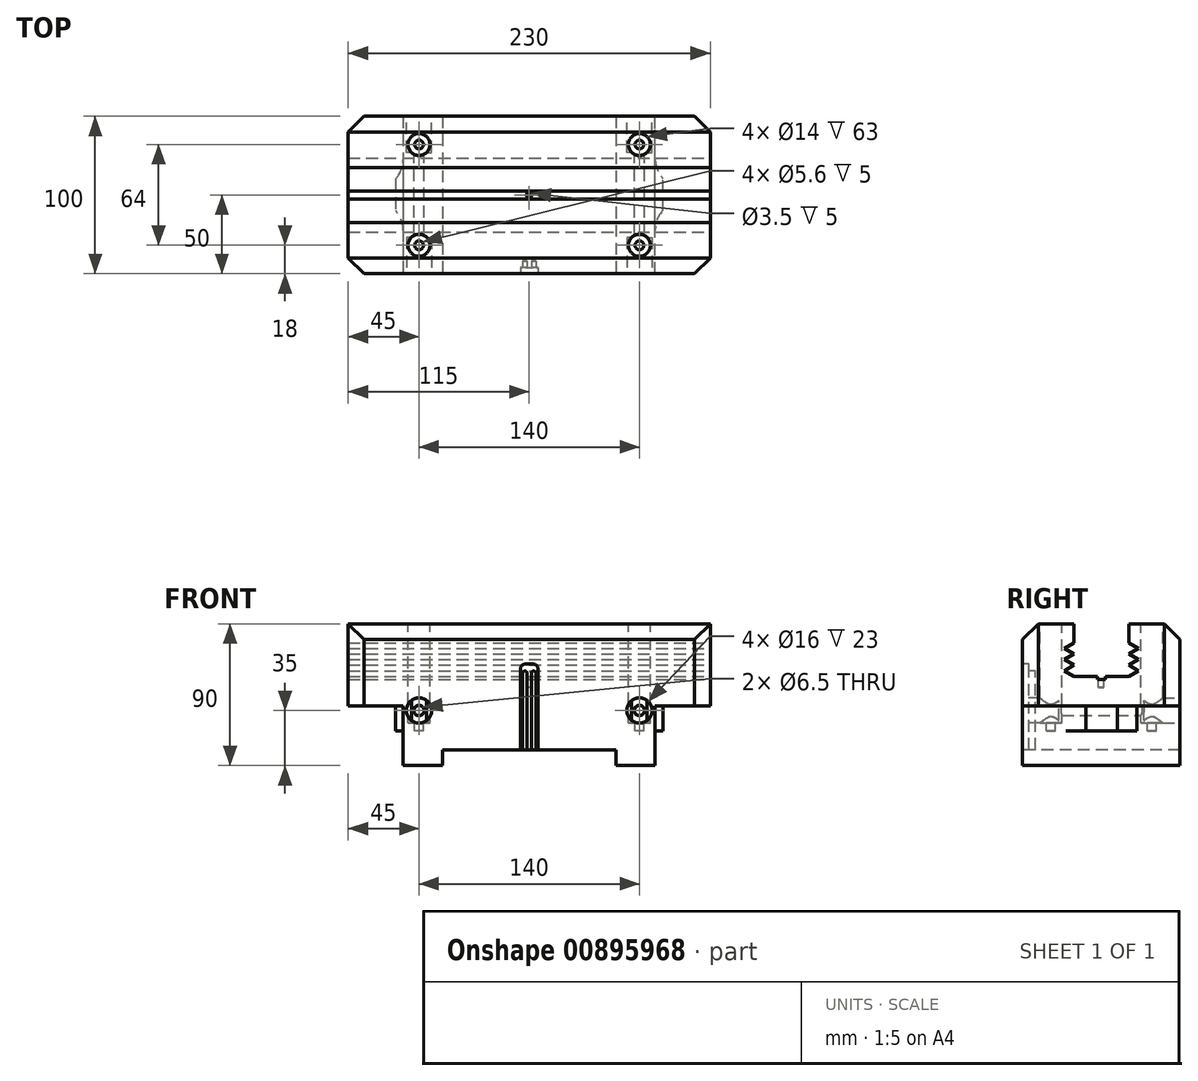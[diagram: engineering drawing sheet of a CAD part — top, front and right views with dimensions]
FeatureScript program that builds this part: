
annotation { "Feature Type Name" : "Feature", "Feature Type Description" : "" }
export const myFeature = defineFeature(function(context is Context, id is Id, definition is map)
    precondition{}
    {
        {
            var Q0;
            Q0=qCreatedBy(makeId("Top.planeOp"),FACE);
            var sketch = newSketch(context, id + "F0", { "sketchPlane" : qUnion([Q0])});
            skLineSegment(sketch, "E0.bottom", {"start": v(-115, 50) * mm, "end": v(115, 50) * mm});
            skLineSegment(sketch, "E0.top", {"start": v(-115, -50) * mm, "end": v(115, -50) * mm});
            skLineSegment(sketch, "E0.left", {"start": v(-115, 50) * mm, "end": v(-115, -50) * mm});
            skLineSegment(sketch, "E0.right", {"start": v(115, 50) * mm, "end": v(115, -50) * mm});
            skSolve(sketch);
        }
        {
            var Q0;
            Q0=makeQuery(id+"F0.imprint","IMPRINT",FACE,{"disambiguationData":[TD([[makeQuery(id+"F0.imprint","IMPRINT",EDGE,{"derivedFrom":sQuery(id+"F0.wireOp",EDGE,"E0.bottom")}),-1.0]])]});
            extrude(context, id + "F1", {"entities" : qUnion([Q0]), "oppositeDirection" : true, "depth" : 52 * mm, "offsetDistance" : 25 * mm});
        }
        {
            var Q0;
            Q0=makeQuery(id+"F1.opExtrude","SWEPT_FACE",FACE,{"disambiguationData":[OSD([sQuery(id+"F0.wireOp",EDGE,"E0.right")])]});
            var sketch = newSketch(context, id + "F2", { "sketchPlane" : qUnion([Q0])});
            skLineSegment(sketch, "E1", {"start": v(-17.5, 0) * mm, "end": v(17.5, 0) * mm});
            skLineSegment(sketch, "E2", {"start": v(-17.5, 0) * mm, "end": v(-17.5, -12) * mm});
            skLineSegment(sketch, "E3", {"start": v(-17.5, -12) * mm, "end": v(-23.52, -15.55) * mm});
            skLineSegment(sketch, "E4", {"start": v(-23.52, -15.55) * mm, "end": v(-17.5, -19.1) * mm});
            skLineSegment(sketch, "E5", {"start": v(-17.5, -19.1) * mm, "end": v(-23.52, -22.65) * mm});
            skLineSegment(sketch, "E6", {"start": v(-23.52, -22.65) * mm, "end": v(-17.5, -26.2) * mm});
            skLineSegment(sketch, "E7", {"start": v(-17.5, -26.2) * mm, "end": v(-23.52, -29.75) * mm});
            skLineSegment(sketch, "E8", {"start": v(-23.52, -29.75) * mm, "end": v(-17.5, -33.3) * mm});
            skLineSegment(sketch, "E9", {"start": v(17.5, 0) * mm, "end": v(17.5, -12) * mm});
            skLineSegment(sketch, "E10", {"start": v(17.5, -33.3) * mm, "end": v(23.52, -29.75) * mm});
            skLineSegment(sketch, "E11", {"start": v(23.52, -29.75) * mm, "end": v(17.5, -26.2) * mm});
            skLineSegment(sketch, "E12", {"start": v(17.5, -26.2) * mm, "end": v(23.52, -22.65) * mm});
            skLineSegment(sketch, "E13", {"start": v(23.52, -22.65) * mm, "end": v(17.5, -19.1) * mm});
            skLineSegment(sketch, "E14", {"start": v(17.5, -19.1) * mm, "end": v(23.52, -15.55) * mm});
            skLineSegment(sketch, "E15", {"start": v(23.52, -15.55) * mm, "end": v(17.5, -12) * mm});
            skLineSegment(sketch, "E16", {"start": v(-17.5, -33.3) * mm, "end": v(-2.5, -33.3) * mm});
            skLineSegment(sketch, "E17", {"start": v(17.5, -33.3) * mm, "end": v(2.5, -33.3) * mm});
            skLineSegment(sketch, "E18", {"start": v(-2.5, -33.3) * mm, "end": v(-2.5, -35.3) * mm});
            skLineSegment(sketch, "E19", {"start": v(2.5, -33.3) * mm, "end": v(2.5, -35.3) * mm});
            skLineSegment(sketch, "E20", {"start": v(2.5, -35.3) * mm, "end": v(-2.5, -35.3) * mm});
            skSolve(sketch);
        }
        {
            var Q0;
            Q0=makeQuery(id+"F2.imprint","IMPRINT",FACE,{"disambiguationData":[TD([[makeQuery(id+"F2.imprint","IMPRINT",EDGE,{"derivedFrom":sQuery(id+"F2.wireOp",EDGE,"E1")}),1.0]])]});
            extrude(context, id + "F3", {"entities" : qUnion([Q0]), "operationType" : NewBodyOperationType.REMOVE, "endBound" : BoundingType.UP_TO_NEXT, "oppositeDirection" : true, "depth" : 218 * mm, "offsetDistance" : 25 * mm});
        }
        {
            var Q0;
            Q0=makeQuery(id+"F1.opExtrude","CAP_EDGE",EDGE,{"disambiguationData":[OSD([sQuery(id+"F0.wireOp",EDGE,"E0.bottom")])],"isStart":true});
            var Q1;
            Q1=makeQuery(id+"F1.opExtrude","CAP_EDGE",EDGE,{"disambiguationData":[OSD([sQuery(id+"F0.wireOp",EDGE,"E0.top")])],"isStart":true});
            var Q2;
            Q2=makeQuery(id+"F1.opExtrude","SWEPT_EDGE",EDGE,{"disambiguationData":[OSD([sQuery(id+"F0.wireOp",EDGE,"E0.top"),sQuery(id+"F0.wireOp",EDGE,"E0.right")])]});
            var Q3;
            Q3=makeQuery(id+"F1.opExtrude","SWEPT_EDGE",EDGE,{"disambiguationData":[OSD([sQuery(id+"F0.wireOp",EDGE,"E0.bottom"),sQuery(id+"F0.wireOp",EDGE,"E0.right")])]});
            var Q4;
            Q4=makeQuery(id+"F1.opExtrude","SWEPT_EDGE",EDGE,{"disambiguationData":[OSD([sQuery(id+"F0.wireOp",EDGE,"E0.top"),sQuery(id+"F0.wireOp",EDGE,"E0.left")])]});
            var Q5;
            Q5=makeQuery(id+"F1.opExtrude","SWEPT_EDGE",EDGE,{"disambiguationData":[OSD([sQuery(id+"F0.wireOp",EDGE,"E0.bottom"),sQuery(id+"F0.wireOp",EDGE,"E0.left")])]});
            chamfer(context, id + "F4", {"entities" : qUnion([Q0, Q1, Q2, Q3, Q4, Q5]), "width" : 10 * mm, "tangentPropagation" : true});
        }
        {
            var Q0;
            Q0=makeQuery(id+"F1.opExtrude","CAP_FACE",FACE,{"disambiguationData":[OSD([sQuery(id+"F0.wireOp",EDGE,"E0.bottom"),sQuery(id+"F0.wireOp",EDGE,"E0.top"),sQuery(id+"F0.wireOp",EDGE,"E0.left"),sQuery(id+"F0.wireOp",EDGE,"E0.right")])],"isStart":false});
            var sketch = newSketch(context, id + "F5", { "sketchPlane" : qUnion([Q0])});
            skLineSegment(sketch, "E21", {"start": v(80, 50) * mm, "end": v(80, -50) * mm});
            skLineSegment(sketch, "E22", {"start": v(80, -50) * mm, "end": v(-80, -50) * mm});
            skLineSegment(sketch, "E23", {"start": v(-80, -50) * mm, "end": v(-80, 50) * mm});
            skLineSegment(sketch, "E24", {"start": v(-80, 50) * mm, "end": v(80, 50) * mm});
            skSolve(sketch);
        }
        {
            var Q0;
            Q0=makeQuery(id+"F5.imprint","IMPRINT",FACE,{"disambiguationData":[TD([[makeQuery(id+"F5.imprint","IMPRINT",EDGE,{"derivedFrom":sQuery(id+"F5.wireOp",EDGE,"E21")}),-1.0]])]});
            extrude(context, id + "F6", {"entities" : qUnion([Q0]), "operationType" : NewBodyOperationType.ADD, "depth" : 38 * mm, "offsetDistance" : 25 * mm});
        }
        {
            var Q0;
            {var subQ0=sQuery(id+"F0.wireOp",EDGE,"E0.bottom");var subQ1=sQuery(id+"F0.wireOp",EDGE,"E0.right");var subQ2=sQuery(id+"F0.wireOp",EDGE,"E0.left");Q0=makeQuery(id+"F3.boolean.opBoolean","SPLIT",FACE,{"disambiguationData":[TD([makeQuery(id+"F1.opExtrude","SWEPT_FACE",FACE,{"disambiguationData":[OSD([subQ0])]})])],"derivedFrom":makeQuery(id+"F1.opExtrude","CAP_FACE",FACE,{"disambiguationData":[OSD([subQ0,sQuery(id+"F0.wireOp",EDGE,"E0.top"),subQ2,subQ1])],"isStart":true})});}
            var sketch = newSketch(context, id + "F7", { "sketchPlane" : qUnion([Q0])});
            skCircle(sketch, "E25", {"center": v(70, -32) * mm, "radius": 7 * mm});
            skCircle(sketch, "E26", {"center": v(-70, -32) * mm, "radius": 7 * mm});
            skCircle(sketch, "E27", {"center": v(-70, 32) * mm, "radius": 7 * mm});
            skCircle(sketch, "E28", {"center": v(70, 32) * mm, "radius": 7 * mm});
            skCircle(sketch, "E29", {"center": v(-70, 32) * mm, "radius": 2.8 * mm});
            skCircle(sketch, "E30", {"center": v(70, 32) * mm, "radius": 2.8 * mm});
            skCircle(sketch, "E31", {"center": v(70, -32) * mm, "radius": 2.8 * mm});
            skCircle(sketch, "E32", {"center": v(-70, -32) * mm, "radius": 2.8 * mm});
            skSolve(sketch);
        }
        {
            var Q0;
            Q0 = qSketchRegion(id + "F7", true);
            extrude(context, id + "F8", {"entities" : qUnion([Q0]), "operationType" : NewBodyOperationType.REMOVE, "oppositeDirection" : true, "depth" : 63 * mm, "offsetDistance" : 25 * mm});
        }
        {
            var Q0;
            {var subQ0=sQuery(id+"F0.wireOp",EDGE,"E0.bottom");var subQ1=sQuery(id+"F0.wireOp",EDGE,"E0.right");var subQ2=sQuery(id+"F0.wireOp",EDGE,"E0.left");Q0=makeQuery(id+"F8.boolean.opBoolean","SPLIT",FACE,{"disambiguationData":[TD([makeQuery(id+"F8.opExtrude","SWEPT_FACE",FACE,{"disambiguationData":[OSD([sQuery(id+"F7.wireOp",EDGE,"E30")])]})])],"derivedFrom":makeQuery(id+"F3.boolean.opBoolean","SPLIT",FACE,{"disambiguationData":[TD([makeQuery(id+"F1.opExtrude","SWEPT_FACE",FACE,{"disambiguationData":[OSD([subQ0])]})])],"derivedFrom":makeQuery(id+"F1.opExtrude","CAP_FACE",FACE,{"disambiguationData":[OSD([subQ0,sQuery(id+"F0.wireOp",EDGE,"E0.top"),subQ2,subQ1])],"isStart":true})})});}
            var Q1;
            {var subQ0=sQuery(id+"F0.wireOp",EDGE,"E0.bottom");var subQ1=sQuery(id+"F0.wireOp",EDGE,"E0.right");var subQ2=sQuery(id+"F0.wireOp",EDGE,"E0.left");Q1=makeQuery(id+"F8.boolean.opBoolean","SPLIT",FACE,{"disambiguationData":[TD([makeQuery(id+"F8.opExtrude","SWEPT_FACE",FACE,{"disambiguationData":[OSD([sQuery(id+"F7.wireOp",EDGE,"E29")])]})])],"derivedFrom":makeQuery(id+"F3.boolean.opBoolean","SPLIT",FACE,{"disambiguationData":[TD([makeQuery(id+"F1.opExtrude","SWEPT_FACE",FACE,{"disambiguationData":[OSD([subQ0])]})])],"derivedFrom":makeQuery(id+"F1.opExtrude","CAP_FACE",FACE,{"disambiguationData":[OSD([subQ0,sQuery(id+"F0.wireOp",EDGE,"E0.top"),subQ2,subQ1])],"isStart":true})})});}
            var Q2;
            {var subQ0=sQuery(id+"F0.wireOp",EDGE,"E0.top");var subQ1=sQuery(id+"F0.wireOp",EDGE,"E0.left");var subQ2=sQuery(id+"F0.wireOp",EDGE,"E0.right");Q2=makeQuery(id+"F8.boolean.opBoolean","SPLIT",FACE,{"disambiguationData":[TD([makeQuery(id+"F8.opExtrude","SWEPT_FACE",FACE,{"disambiguationData":[OSD([sQuery(id+"F7.wireOp",EDGE,"E32")])]})])],"derivedFrom":makeQuery(id+"F3.boolean.opBoolean","SPLIT",FACE,{"disambiguationData":[TD([makeQuery(id+"F1.opExtrude","SWEPT_FACE",FACE,{"disambiguationData":[OSD([subQ0])]})])],"derivedFrom":makeQuery(id+"F1.opExtrude","CAP_FACE",FACE,{"disambiguationData":[OSD([sQuery(id+"F0.wireOp",EDGE,"E0.bottom"),subQ0,subQ1,subQ2])],"isStart":true})})});}
            var Q3;
            {var subQ0=sQuery(id+"F0.wireOp",EDGE,"E0.top");var subQ1=sQuery(id+"F0.wireOp",EDGE,"E0.left");var subQ2=sQuery(id+"F0.wireOp",EDGE,"E0.right");Q3=makeQuery(id+"F8.boolean.opBoolean","SPLIT",FACE,{"disambiguationData":[TD([makeQuery(id+"F8.opExtrude","SWEPT_FACE",FACE,{"disambiguationData":[OSD([sQuery(id+"F7.wireOp",EDGE,"E31")])]})])],"derivedFrom":makeQuery(id+"F3.boolean.opBoolean","SPLIT",FACE,{"disambiguationData":[TD([makeQuery(id+"F1.opExtrude","SWEPT_FACE",FACE,{"disambiguationData":[OSD([subQ0])]})])],"derivedFrom":makeQuery(id+"F1.opExtrude","CAP_FACE",FACE,{"disambiguationData":[OSD([sQuery(id+"F0.wireOp",EDGE,"E0.bottom"),subQ0,subQ1,subQ2])],"isStart":true})})});}
            extrude(context, id + "F9", {"entities" : qUnion([Q0, Q1, Q2, Q3]), "operationType" : NewBodyOperationType.REMOVE, "oppositeDirection" : true, "depth" : 68 * mm, "offsetDistance" : 25 * mm});
        }
        {
            var Q0;
            Q0=makeQuery(id+"F6.boolean.opBoolean","MERGE",FACE,{"derivedFrom":[makeQuery(id+"F1.opExtrude","SWEPT_FACE",FACE,{"disambiguationData":[OSD([sQuery(id+"F0.wireOp",EDGE,"E0.bottom")])]}),makeQuery(id+"F6.opExtrude","SWEPT_FACE",FACE,{"disambiguationData":[OSD([sQuery(id+"F5.wireOp",EDGE,"E22")])]})]});
            var sketch = newSketch(context, id + "F10", { "sketchPlane" : qUnion([Q0])});
            skCircle(sketch, "E33", {"center": v(70, -55) * mm, "radius": 8 * mm});
            skCircle(sketch, "E34", {"center": v(-70, -55) * mm, "radius": 8 * mm});
            skCircle(sketch, "E35", {"center": v(70, -55) * mm, "radius": 3.25 * mm});
            skCircle(sketch, "E36", {"center": v(-70, -55) * mm, "radius": 3.25 * mm});
            skSolve(sketch);
        }
        {
            var Q0;
            Q0 = qSketchRegion(id + "F10", true);
            extrude(context, id + "F11", {"entities" : qUnion([Q0]), "operationType" : NewBodyOperationType.REMOVE, "oppositeDirection" : true, "depth" : 23 * mm, "offsetDistance" : 25 * mm});
        }
        {
            var Q0;
            Q0=makeQuery(id+"F11.boolean.opBoolean","SPLIT",FACE,{"disambiguationData":[TD([makeQuery(id+"F11.opExtrude","SWEPT_FACE",FACE,{"disambiguationData":[OSD([sQuery(id+"F10.wireOp",EDGE,"E36")])]})])],"derivedFrom":makeQuery(id+"F6.boolean.opBoolean","MERGE",FACE,{"derivedFrom":[makeQuery(id+"F1.opExtrude","SWEPT_FACE",FACE,{"disambiguationData":[OSD([sQuery(id+"F0.wireOp",EDGE,"E0.bottom")])]}),makeQuery(id+"F6.opExtrude","SWEPT_FACE",FACE,{"disambiguationData":[OSD([sQuery(id+"F5.wireOp",EDGE,"E22")])]})]})});
            var Q1;
            Q1=makeQuery(id+"F11.boolean.opBoolean","SPLIT",FACE,{"disambiguationData":[TD([makeQuery(id+"F11.opExtrude","SWEPT_FACE",FACE,{"disambiguationData":[OSD([sQuery(id+"F10.wireOp",EDGE,"E35")])]})])],"derivedFrom":makeQuery(id+"F6.boolean.opBoolean","MERGE",FACE,{"derivedFrom":[makeQuery(id+"F1.opExtrude","SWEPT_FACE",FACE,{"disambiguationData":[OSD([sQuery(id+"F0.wireOp",EDGE,"E0.bottom")])]}),makeQuery(id+"F6.opExtrude","SWEPT_FACE",FACE,{"disambiguationData":[OSD([sQuery(id+"F5.wireOp",EDGE,"E22")])]})]})});
            extrude(context, id + "F12", {"entities" : qUnion([Q0, Q1]), "operationType" : NewBodyOperationType.REMOVE, "oppositeDirection" : true, "depth" : 179.1 * mm, "offsetDistance" : 25 * mm});
        }
        {
            var Q0;
            Q0=makeQuery(id+"F6.boolean.opBoolean","MERGE",FACE,{"derivedFrom":[makeQuery(id+"F1.opExtrude","SWEPT_FACE",FACE,{"disambiguationData":[OSD([sQuery(id+"F0.wireOp",EDGE,"E0.top")])]}),makeQuery(id+"F6.opExtrude","SWEPT_FACE",FACE,{"disambiguationData":[OSD([sQuery(id+"F5.wireOp",EDGE,"E24")])]})]});
            var sketch = newSketch(context, id + "F13", { "sketchPlane" : qUnion([Q0])});
            skCircle(sketch, "E37", {"center": v(-70, -55) * mm, "radius": 8 * mm});
            skCircle(sketch, "E38", {"center": v(-70, -55) * mm, "radius": 3.25 * mm});
            skCircle(sketch, "E39", {"center": v(70, -55) * mm, "radius": 8 * mm});
            skCircle(sketch, "E40", {"center": v(70, -55) * mm, "radius": 3.25 * mm});
            skLineSegment(sketch, "E41.bottom", {"start": v(-55, -90) * mm, "end": v(55, -90) * mm});
            skLineSegment(sketch, "E41.top", {"start": v(-55, -80) * mm, "end": v(55, -80) * mm});
            skLineSegment(sketch, "E41.left", {"start": v(-55, -90) * mm, "end": v(-55, -80) * mm});
            skLineSegment(sketch, "E41.right", {"start": v(55, -90) * mm, "end": v(55, -80) * mm});
            skSolve(sketch);
        }
        {
            var Q0;
            Q0 = qSketchRegion(id + "F13", true);
            extrude(context, id + "F14", {"entities" : qUnion([Q0]), "operationType" : NewBodyOperationType.REMOVE, "oppositeDirection" : true, "depth" : 23 * mm, "offsetDistance" : 25 * mm});
        }
        {
            var Q0;
            Q0=makeQuery(id+"F13.imprint","IMPRINT",FACE,{"disambiguationData":[TD([[makeQuery(id+"F13.imprint","IMPRINT",EDGE,{"derivedFrom":sQuery(id+"F13.wireOp",EDGE,"E41.bottom")}),1.0]])]});
            extrude(context, id + "F15", {"entities" : qUnion([Q0]), "operationType" : NewBodyOperationType.REMOVE, "endBound" : BoundingType.THROUGH_ALL, "oppositeDirection" : true, "depth" : 25 * mm, "offsetDistance" : 25 * mm});
        }
        {
            var Q0;
            Q0=makeQuery(id+"F6.opExtrude","SWEPT_FACE",FACE,{"disambiguationData":[OSD([sQuery(id+"F5.wireOp",EDGE,"E23")])]});
            var sketch = newSketch(context, id + "F16", { "sketchPlane" : qUnion([Q0])});
            skLineSegment(sketch, "E42.bottom", {"start": v(-22.5, -52) * mm, "end": v(22.5, -52) * mm});
            skLineSegment(sketch, "E42.top", {"start": v(-22.5, -68) * mm, "end": v(22.5, -68) * mm});
            skLineSegment(sketch, "E42.left", {"start": v(-22.5, -52) * mm, "end": v(-22.5, -68) * mm});
            skLineSegment(sketch, "E42.right", {"start": v(22.5, -52) * mm, "end": v(22.5, -68) * mm});
            skSolve(sketch);
        }
        {
            var Q0;
            Q0=makeQuery(id+"F16.imprint","IMPRINT",FACE,{"disambiguationData":[TD([[makeQuery(id+"F16.imprint","IMPRINT",EDGE,{"derivedFrom":sQuery(id+"F16.wireOp",EDGE,"E42.bottom")}),-1.0]])]});
            extrude(context, id + "F17", {"entities" : qUnion([Q0]), "operationType" : NewBodyOperationType.ADD, "depth" : 5 * mm, "offsetDistance" : 25 * mm});
        }
        {
            var Q0;
            Q0=makeQuery(id+"F17.opExtrude","SWEPT_FACE",FACE,{"disambiguationData":[OSD([sQuery(id+"F16.wireOp",EDGE,"E42.top")])]});
            var sketch = newSketch(context, id + "F18", { "sketchPlane" : qUnion([Q0])});
            skLineSegment(sketch, "E43", {"start": v(-85, 10) * mm, "end": v(-85, -10) * mm});
            skArc(sketch, "E44", {"start": v(-80, -22.5) * mm, "mid": v(-81.3, -15.77) * mm, "end": v(-85, -10) * mm});
            skArc(sketch, "E45", {"start": v(-85, 10) * mm, "mid": v(-81.3, 15.77) * mm, "end": v(-80, 22.5) * mm});
            skSolve(sketch);
        }
        {
            var Q0;
            Q0 = qSketchRegion(id + "F18", true);
            var Q1;
            {var subQ0=sQuery(id+"F18.wireOp",EDGE,"E44");Q1=makeQuery(id+"F18.imprint","IMPRINT",FACE,{"disambiguationData":[TD([[makeQuery(id+"F18.imprint","IMPRINT",EDGE,{"derivedFrom":subQ0}),1.0]])]});}
            var Q2;
            {var subQ0=sQuery(id+"F18.wireOp",EDGE,"E45");Q2=makeQuery(id+"F18.imprint","IMPRINT",FACE,{"disambiguationData":[TD([[makeQuery(id+"F18.imprint","IMPRINT",EDGE,{"derivedFrom":subQ0}),1.0]])]});}
            extrude(context, id + "F19", {"entities" : qUnion([Q0, Q1, Q2]), "operationType" : NewBodyOperationType.REMOVE, "oppositeDirection" : true, "depth" : 16 * mm, "offsetDistance" : 25 * mm});
        }
        {
            var Q0;
            Q0=makeQuery(id+"F6.opExtrude","SWEPT_FACE",FACE,{"disambiguationData":[OSD([sQuery(id+"F5.wireOp",EDGE,"E21")])]});
            var sketch = newSketch(context, id + "F20", { "sketchPlane" : qUnion([Q0])});
            skLineSegment(sketch, "E46.bottom", {"start": v(-22.5, -52) * mm, "end": v(22.5, -52) * mm});
            skLineSegment(sketch, "E46.top", {"start": v(-22.5, -68) * mm, "end": v(22.5, -68) * mm});
            skLineSegment(sketch, "E46.left", {"start": v(-22.5, -52) * mm, "end": v(-22.5, -68) * mm});
            skLineSegment(sketch, "E46.right", {"start": v(22.5, -52) * mm, "end": v(22.5, -68) * mm});
            skSolve(sketch);
        }
        {
            var Q0;
            Q0=makeQuery(id+"F20.imprint","IMPRINT",FACE,{"disambiguationData":[TD([[makeQuery(id+"F20.imprint","IMPRINT",EDGE,{"derivedFrom":sQuery(id+"F20.wireOp",EDGE,"E46.bottom")}),-1.0]])]});
            extrude(context, id + "F21", {"entities" : qUnion([Q0]), "operationType" : NewBodyOperationType.ADD, "depth" : 5 * mm, "offsetDistance" : 25 * mm});
        }
        {
            var Q0;
            Q0=makeQuery(id+"F21.opExtrude","SWEPT_FACE",FACE,{"disambiguationData":[OSD([sQuery(id+"F20.wireOp",EDGE,"E46.top")])]});
            var sketch = newSketch(context, id + "F22", { "sketchPlane" : qUnion([Q0])});
            skLineSegment(sketch, "E47", {"start": v(85, -10.3) * mm, "end": v(85, 9.7) * mm});
            skArc(sketch, "E48", {"start": v(80, 22.5) * mm, "mid": v(81.3, 15.63) * mm, "end": v(85, 9.7) * mm});
            skArc(sketch, "E49", {"start": v(85, -10.3) * mm, "mid": v(81.35, -15.93) * mm, "end": v(80, -22.5) * mm});
            skSolve(sketch);
        }
        {
            var Q0;
            Q0 = qSketchRegion(id + "F22", true);
            var Q1;
            {var subQ0=sQuery(id+"F22.wireOp",EDGE,"E49");Q1=makeQuery(id+"F22.imprint","IMPRINT",FACE,{"disambiguationData":[TD([[makeQuery(id+"F22.imprint","IMPRINT",EDGE,{"derivedFrom":subQ0}),1.0]])]});}
            var Q2;
            {var subQ0=sQuery(id+"F22.wireOp",EDGE,"E48");Q2=makeQuery(id+"F22.imprint","IMPRINT",FACE,{"disambiguationData":[TD([[makeQuery(id+"F22.imprint","IMPRINT",EDGE,{"derivedFrom":subQ0}),1.0]])]});}
            extrude(context, id + "F23", {"entities" : qUnion([Q0, Q1, Q2]), "operationType" : NewBodyOperationType.REMOVE, "oppositeDirection" : true, "depth" : 16 * mm, "offsetDistance" : 25 * mm});
        }
        {
            var Q0;
            Q0=makeQuery(id+"F6.boolean.opBoolean","MERGE",FACE,{"derivedFrom":[makeQuery(id+"F1.opExtrude","SWEPT_FACE",FACE,{"disambiguationData":[OSD([sQuery(id+"F0.wireOp",EDGE,"E0.top")])]}),makeQuery(id+"F6.opExtrude","SWEPT_FACE",FACE,{"disambiguationData":[OSD([sQuery(id+"F5.wireOp",EDGE,"E24")])]})]});
            var sketch = newSketch(context, id + "F24", { "sketchPlane" : qUnion([Q0])});
            skLineSegment(sketch, "E50.bottom", {"start": v(-5.5, -80) * mm, "end": v(5.5, -80) * mm});
            skLineSegment(sketch, "E50.left", {"start": v(-5.5, -80) * mm, "end": v(-5.5, -31) * mm});
            skLineSegment(sketch, "E50.right", {"start": v(5.5, -80) * mm, "end": v(5.5, -31) * mm});
            skLineSegment(sketch, "E51.top", {"start": v(-2.5, -25.5) * mm, "end": v(2.5, -25.5) * mm});
            skLineSegment(sketch, "E51.left", {"start": v(-5.5, -31) * mm, "end": v(-5.5, -28.5) * mm});
            skLineSegment(sketch, "E51.right", {"start": v(5.5, -31) * mm, "end": v(5.5, -28.5) * mm});
            skPoint(sketch, "E52.visualSharp", {"position": v(5.5, -25.5) * mm});
            skArc(sketch, "E52.filletArc", {"start": v(5.5, -28.5) * mm, "mid": v(4.62, -26.38) * mm, "end": v(2.5, -25.5) * mm});
            skPoint(sketch, "E53.visualSharp", {"position": v(-5.5, -25.5) * mm});
            skArc(sketch, "E53.filletArc", {"start": v(-2.5, -25.5) * mm, "mid": v(-4.62, -26.38) * mm, "end": v(-5.5, -28.5) * mm});
            skSolve(sketch);
        }
        {
            var Q0;
            Q0=makeQuery(id+"F24.imprint","IMPRINT",FACE,{"disambiguationData":[TD([[makeQuery(id+"F24.imprint","IMPRINT",EDGE,{"derivedFrom":sQuery(id+"F24.wireOp",EDGE,"E50.bottom")}),1.0]])]});
            extrude(context, id + "F25", {"entities" : qUnion([Q0]), "operationType" : NewBodyOperationType.REMOVE, "oppositeDirection" : true, "depth" : 4 * mm, "offsetDistance" : 25 * mm});
        }
        {
            var Q0;
            Q0=makeQuery(id+"F25.boolean.opBoolean","COPY",FACE,{"derivedFrom":makeQuery(id+"F25.opExtrude","CAP_FACE",FACE,{"disambiguationData":[OSD([sQuery(id+"F24.wireOp",EDGE,"E50.bottom"),sQuery(id+"F24.wireOp",EDGE,"E50.left"),sQuery(id+"F24.wireOp",EDGE,"E50.right"),sQuery(id+"F24.wireOp",EDGE,"E51.top"),sQuery(id+"F24.wireOp",EDGE,"E51.left"),sQuery(id+"F24.wireOp",EDGE,"E51.right"),sQuery(id+"F24.wireOp",EDGE,"E52.filletArc"),sQuery(id+"F24.wireOp",EDGE,"E53.filletArc")])],"isStart":false})});
            var sketch = newSketch(context, id + "F26", { "sketchPlane" : qUnion([Q0])});
            skLineSegment(sketch, "E54.bottom", {"start": v(1.3, -80) * mm, "end": v(4.3, -80) * mm});
            skLineSegment(sketch, "E54.left", {"start": v(1.3, -80) * mm, "end": v(1.3, -31.5) * mm});
            skLineSegment(sketch, "E54.right", {"start": v(4.3, -80) * mm, "end": v(4.3, -31.5) * mm});
            skLineSegment(sketch, "E55.bottom", {"start": v(-4.3, -80) * mm, "end": v(-1.3, -80) * mm});
            skLineSegment(sketch, "E55.left", {"start": v(-4.3, -80) * mm, "end": v(-4.3, -31.5) * mm});
            skLineSegment(sketch, "E55.right", {"start": v(-1.3, -80) * mm, "end": v(-1.3, -31.5) * mm});
            skArc(sketch, "E56", {"start": v(4.3, -31.5) * mm, "mid": v(2.8, -30) * mm, "end": v(1.3, -31.5) * mm});
            skArc(sketch, "E57", {"start": v(-1.3, -31.5) * mm, "mid": v(-2.8, -30) * mm, "end": v(-4.3, -31.5) * mm});
            skSolve(sketch);
        }
        {
            var Q0;
            Q0 = qSketchRegion(id + "F26", true);
            extrude(context, id + "F27", {"entities" : qUnion([Q0]), "operationType" : NewBodyOperationType.REMOVE, "oppositeDirection" : true, "depth" : 4 * mm, "offsetDistance" : 25 * mm});
        }
        {
            var Q0;
            Q0=makeQuery(id+"F3.boolean.opBoolean","COPY",FACE,{"derivedFrom":makeQuery(id+"F3.opExtrude","SWEPT_FACE",FACE,{"disambiguationData":[OSD([sQuery(id+"F2.wireOp",EDGE,"E20")])]})});
            var sketch = newSketch(context, id + "F28", { "sketchPlane" : qUnion([Q0])});
            skCircle(sketch, "E58", {"center": v(0, 0) * mm, "radius": 1.75 * mm});
            skSolve(sketch);
        }
        {
            var Q0;
            Q0 = qSketchRegion(id + "F28", true);
            extrude(context, id + "F29", {"entities" : qUnion([Q0]), "operationType" : NewBodyOperationType.REMOVE, "oppositeDirection" : true, "depth" : 5 * mm, "offsetDistance" : 25 * mm});
        }
    });
